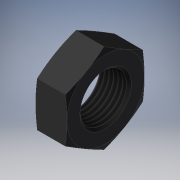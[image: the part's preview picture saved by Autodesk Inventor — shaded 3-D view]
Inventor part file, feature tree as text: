
AUTODESK INVENTOR PART (.ipt)
format: ipt  version: 2019 (Build 230136000, 136)  size: 164,352 bytes
history: native  units: mm
features: other x21, sketch x3, revolve x2, extrude x1, thread x1
ambient origin geometry x8: Origin, YZ Plane, XZ Plane, XY Plane, X Axis, Y Axis, Z Axis, Center Point
bodies: Solid1 (feature_tree)
feature tree (28):
  revolve  "Revolution1"  [1 undecoded]
  extrude  "Extrusion1"  Depth=8.12546mm TaperAngle=0.0deg
  revolve  "Revolution2"  [1 undecoded]
  thread  "Thread1"  [1 undecoded]
  other  "c_XY"
  other  "c_YZ"
  other  "c_ZX"
  other  "c_X"
  other  "c_Y"
  other  "c_Z"
  other  "c_Center"
  other  "kb_XY"
  other  "kb_YZ"
  other  "kb_ZX"
  other  "kb_X"
  other  "kb_Y"
  other  "kb_Z"
  other  "kb_Center"
  other  "nut_XY"
  other  "nut_YZ"
  other  "nut_ZX"
  other  "nut_X"
  other  "nut_Y"
  other  "nut_Z"
  other  "nut_Center"
  sketch  "Sketch_1"  dims[d0=360.0deg d1=9.652mm d2=0.0mm]
  sketch  "Sketch_2"  dims[d3=360.0deg d4=8.12546mm d5=0.0mm]
  sketch  "Sketch_3"  dims[d6=0.0mm d7=0.0mm]
note: 3 required parameter values undecoded (feature->parameter linkage not recoverable at this tier; creation-order binding heuristic only, values carry confidence <= 0.55)